# Revit family: CAME_Турникет_Полноростовой_GUARDIAN_CYLINDER
name_source: partatom
category: Специальное оборудование
units: mm (PartAtom-declared; Revit-internal decimal feet)

## family parameters
Всегда вертикально = Да
На основе рабочей плоскости = Нет
Общий = Нет
При загрузке вырезать с полостями = Нет
Размер круглого соединителя = Использовать диаметр
Тип детали = Нормальный
Точка расчета площади = Нет

## types (1)
- CAME_Турникет_Полноростовой_GUARDIAN_CYLINDER
    ADSK_URL документации изделия = https://camerussia.com
    ADSK_URL страницы изделия = https://camerussia.com
    ADSK_Версия Revit = 2019
    ADSK_Версия семейства = 1.0
    ADSK_Группирование = GUARDIAN
    ADSK_Единица измерения = шт.
    ADSK_Завод-изготовитель = CAME
    ADSK_Классификация нагрузок = Прочее
    ADSK_Код изделия = Код КСР 26.30.50.119.61.2.07.09
    ADSK_Количество = 1
    ADSK_Количество фаз = 1
    ADSK_Коэффициент мощности = 0.96
    ADSK_Марка = АРТ:001CGG SQ AIR
    ADSK_Масса = 0
    ADSK_Наименование = Турникет шлюзовой полноростовой, моторизированный GUARDIAN CYLINDER
    ADSK_Наименование краткое = Турникет GUARDIAN CYLINDER
    ADSK_Напряжение = 230 В
    ADSK_Номинальная мощность = 20 Вт
    ADSK_Обозначение = ТУ 26.30.50-001-89603926-2021
    ADSK_Полная мощность = 21 В·А
    ADSK_Размер_Высота = 2500 мм
    ADSK_Размер_Глубина = 1200 мм
    ADSK_Размер_Ширина = 1200 мм
    BL_BIM library = https://bimlib.pro
    CAME_Диапазон рабочих температур (°C) = -20 ÷ +68
    CAME_Интенсивность использования (%) = ИНТЕНСИВНОЕ
    CAME_Класс защиты (IP) = 44
    CAME_Максимальное количество проходов в минуту = 10-25
    CAME_Напряжение электропитания двигателя (В) = 24 В
    CAME_Тип механизма турникета = моторизованный
    URL = https://camerussia.com
    Группа модели = Турникеты
    Изготовитель = CAME
    Кол = 9
    Описание = Турникет шлюзовой полноростовый для объектов с высоким уровнем безопасности, моторизованный, для прохода в двух направлениях. Корпус из оцинкованной окрашенной стали, IP44. Двери закруглённой формы из многослойного ударопрочного стекла. Анимированный индикатор прохода и направления движения. Подсветка зоны прохода. Встроенный датчик взвешивания. ИК датчик роста. ИК датчк присутствия человека в зоне прохода. Приточная вентиляция. Кнопка аварийного открытия дверей. Совместим с досмотровыми системами и системами поэтапного контроля. Возможность дооснащения видеокамерой распознавания лиц и устройствами идентификации в рамках работы системы контроля доступа. *Опционально доступно пулестойкое стекло (класс B3) и исполнение IP56.
    Шаг = 200 мм
